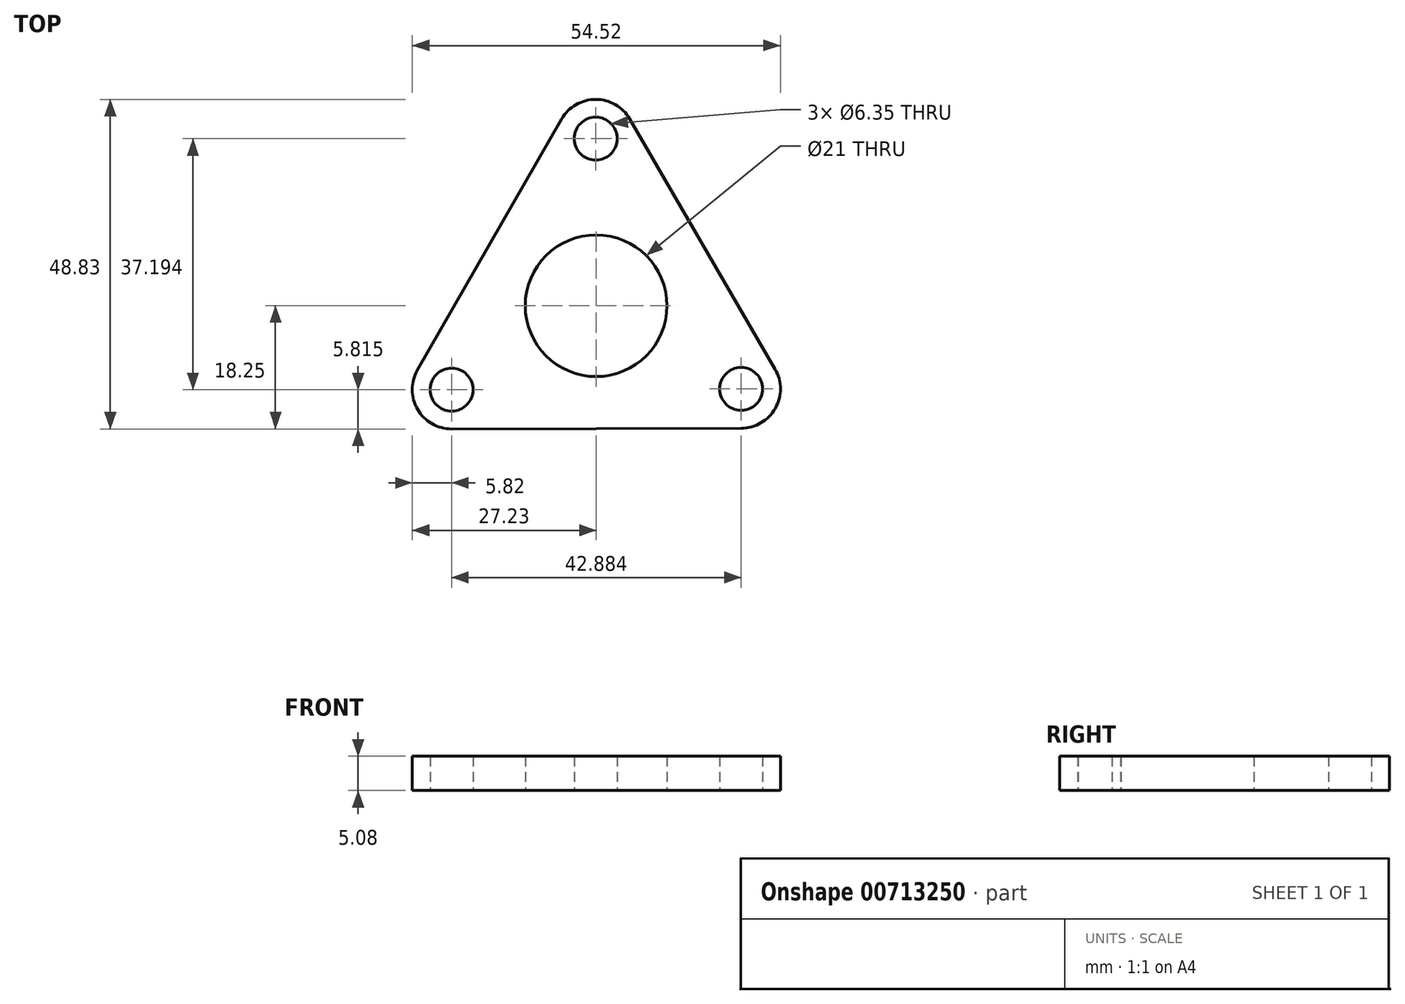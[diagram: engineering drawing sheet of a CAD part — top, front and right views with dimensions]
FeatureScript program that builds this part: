
annotation { "Feature Type Name" : "Feature", "Feature Type Description" : "" }
export const myFeature = defineFeature(function(context is Context, id is Id, definition is map)
    precondition{}
    {
        {
            var Q0;
            Q0=qCreatedBy(makeId("Top.planeOp"),FACE);
            var sketch = newSketch(context, id + "F0", { "sketchPlane" : qUnion([Q0])});
            skCircle(sketch, "E0.cCircle", {"center": v(0, 0) * mm, "radius": 18.2 * mm, "construction": true});
            skLineSegment(sketch, "E0.0", {"start": v(4.97, 27.68) * mm, "end": v(26.5, -9.4) * mm});
            skLineSegment(sketch, "E0.1", {"start": v(21.49, -18.14) * mm, "end": v(-21.4, -18.25) * mm});
            skLineSegment(sketch, "E0.2", {"start": v(-26.46, -9.54) * mm, "end": v(-5.1, 27.65) * mm});
            skPoint(sketch, "E0.0.midPoint", {"position": v(15.74, 9.14) * mm});
            skPoint(sketch, "E1.visualSharp", {"position": v(31.56, -18.12) * mm});
            skArc(sketch, "E1.filletArc", {"start": v(21.49, -18.14) * mm, "mid": v(26.52, -15.22) * mm, "end": v(26.5, -9.4) * mm});
            skPoint(sketch, "E2.visualSharp", {"position": v(-0.1, 36.4) * mm});
            skArc(sketch, "E2.filletArc", {"start": v(4.97, 27.68) * mm, "mid": v(-0.08, 30.58) * mm, "end": v(-5.1, 27.65) * mm});
            skPoint(sketch, "E3.visualSharp", {"position": v(-31.47, -18.28) * mm});
            skArc(sketch, "E3.filletArc", {"start": v(-26.46, -9.54) * mm, "mid": v(-26.44, -15.36) * mm, "end": v(-21.4, -18.25) * mm});
            skSolve(sketch);
        }
        {
            var Q0;
            Q0=makeQuery(id+"F0.imprint","IMPRINT",FACE,{"disambiguationData":[TD([[makeQuery(id+"F0.imprint","IMPRINT",EDGE,{"derivedFrom":sQuery(id+"F0.wireOp",EDGE,"E0.0")}),-1.0]])]});
            extrude(context, id + "F1", {"entities" : qUnion([Q0]), "depth" : 5.08 * mm, "offsetDistance" : 25.4 * mm});
        }
        {
            var Q0;
            Q0=sQuery(id+"F0.wireOp",VERTEX,"E0.cCircle.center");
            var Q1;
            Q1=makeQuery(id+"F1.opExtrude","SWEPT_BODY",BODY,{"disambiguationData":[OSD([sQuery(id+"F0.wireOp",EDGE,"E0.0"),sQuery(id+"F0.wireOp",EDGE,"E0.1"),sQuery(id+"F0.wireOp",EDGE,"E0.2"),sQuery(id+"F0.wireOp",EDGE,"E1.filletArc"),sQuery(id+"F0.wireOp",EDGE,"E2.filletArc"),sQuery(id+"F0.wireOp",EDGE,"E3.filletArc")])]});
            hole(context, id + "F2", {"style" : HoleStyle.SIMPLE, "endStyle" : HoleEndStyle.THROUGH, "oppositeDirection" : true, "holeDiameter" : 21 * mm, "majorDiameter" : 6.35 * mm, "isTappedThrough" : true, "tappedDepth" : 12.7 * mm, "tapClearance" : 3, "locations" : qUnion([Q0]), "scope" : qUnion([Q1])});
        }
        {
            var Q0;
            Q0=sQuery(id+"F0.wireOp",VERTEX,"E3.filletArc.center");
            var Q1;
            Q1=makeQuery(id+"F1.opExtrude","SWEPT_BODY",BODY,{"disambiguationData":[OSD([sQuery(id+"F0.wireOp",EDGE,"E0.0"),sQuery(id+"F0.wireOp",EDGE,"E0.1"),sQuery(id+"F0.wireOp",EDGE,"E0.2"),sQuery(id+"F0.wireOp",EDGE,"E1.filletArc"),sQuery(id+"F0.wireOp",EDGE,"E2.filletArc"),sQuery(id+"F0.wireOp",EDGE,"E3.filletArc")])]});
            hole(context, id + "F3", {"style" : HoleStyle.SIMPLE, "endStyle" : HoleEndStyle.THROUGH, "oppositeDirection" : true, "holeDiameter" : 6.35 * mm, "majorDiameter" : 6.35 * mm, "isTappedThrough" : true, "tappedDepth" : 12.7 * mm, "tapClearance" : 3, "locations" : qUnion([Q0]), "scope" : qUnion([Q1])});
        }
        {
            var Q0;
            Q0=sQuery(id+"F0.wireOp",VERTEX,"E1.filletArc.center");
            var Q1;
            Q1=makeQuery(id+"F1.opExtrude","SWEPT_BODY",BODY,{"disambiguationData":[OSD([sQuery(id+"F0.wireOp",EDGE,"E0.0"),sQuery(id+"F0.wireOp",EDGE,"E0.1"),sQuery(id+"F0.wireOp",EDGE,"E0.2"),sQuery(id+"F0.wireOp",EDGE,"E1.filletArc"),sQuery(id+"F0.wireOp",EDGE,"E2.filletArc"),sQuery(id+"F0.wireOp",EDGE,"E3.filletArc")])]});
            hole(context, id + "F4", {"style" : HoleStyle.SIMPLE, "endStyle" : HoleEndStyle.THROUGH, "oppositeDirection" : true, "holeDiameter" : 6.35 * mm, "majorDiameter" : 6.35 * mm, "isTappedThrough" : true, "tappedDepth" : 12.7 * mm, "tapClearance" : 3, "locations" : qUnion([Q0]), "scope" : qUnion([Q1])});
        }
        {
            var Q0;
            Q0=sQuery(id+"F0.wireOp",VERTEX,"E2.filletArc.center");
            var Q1;
            Q1=makeQuery(id+"F1.opExtrude","SWEPT_BODY",BODY,{"disambiguationData":[OSD([sQuery(id+"F0.wireOp",EDGE,"E0.0"),sQuery(id+"F0.wireOp",EDGE,"E0.1"),sQuery(id+"F0.wireOp",EDGE,"E0.2"),sQuery(id+"F0.wireOp",EDGE,"E1.filletArc"),sQuery(id+"F0.wireOp",EDGE,"E2.filletArc"),sQuery(id+"F0.wireOp",EDGE,"E3.filletArc")])]});
            hole(context, id + "F5", {"style" : HoleStyle.SIMPLE, "endStyle" : HoleEndStyle.THROUGH, "oppositeDirection" : true, "holeDiameter" : 6.35 * mm, "majorDiameter" : 6.35 * mm, "isTappedThrough" : true, "tappedDepth" : 12.7 * mm, "tapClearance" : 3, "locations" : qUnion([Q0]), "scope" : qUnion([Q1])});
        }
    });
